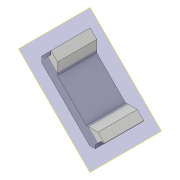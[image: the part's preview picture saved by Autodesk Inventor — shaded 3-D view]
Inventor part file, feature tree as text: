
AUTODESK INVENTOR PART (.ipt)
format: ipt  version: 2019.4 (Build 234330000, 330)  size: 292,864 bytes
history: native  units: mm
features: sketch x5, extrude x4, projected_geometry x4, emboss x2, plane x1
ambient origin geometry x8: Origin, YZ Plane, XZ Plane, XY Plane, X Axis, Y Axis, Z Axis, Center Point
bodies: Solid1 (feature_tree)
feature tree (16):
  extrude  "Extrusion1"  TaperAngle=45.0deg  [1 undecoded]
  plane  "Work Plane1"
  extrude  "Extrusion7"  Depth=30.0mm TaperAngle=0.0deg
  emboss  "Emboss1"
  emboss  "Emboss2"
  extrude  "Extrusion9"  Depth=31.0mm
  extrude  "IM_offset"  Depth=10.0mm TaperAngle=0.0deg
  sketch  "Sketch7"  dims[d0=53.8mm d1=45.0deg]
  projected_geometry  "Projected Loop3"
  sketch  "Sketch10"  dims[d2=6.28mm d3=30.0mm d4=0.0mm]
  sketch  "Sketch11"  dims[d5=8.0mm d28=31.0mm]
  projected_geometry  "Projected Loop6"
  sketch  "Sketch12"  dims[d29=1.3mm d30=10.0mm d31=0.0mm]
  projected_geometry  "Projected Loop7"
  sketch  "Sketch13"  dims[d40=1.5mm d41=1.5mm d42=1.5mm d43=10.0mm d44=10.0mm d45=1.0mm d46=0.0mm d47=120.0deg d48=1.5mm d49=1.5mm d50=1.5mm d51=1.5mm d52=1.5mm d53=0.0mm d54=60.0deg d55=1.5mm d57=120.0deg d58=1.5mm d59=120.0deg d60=1.5mm d63=2.0mm d64=0.0mm d66=10.0mm d67=0.0mm d72=24.0mm d73=45.0deg d74=0.0mm d75=8.267949mm d76=120.0deg d77=8.267949mm d78=4.160254mm d79=5.660254mm d80=120.0deg d81=120.0deg d82=3.0mm d83=3.0mm d84=3.0mm d85=1.5mm d86=7.160254mm d87=7.160254mm d88=4.160254mm d89=1.732051mm d90=5.660254mm d91=1.732051mm d92=4.160254mm d93=0.14mm]
  projected_geometry  "Projected Loop8"
note: 1 required parameter value undecoded (feature->parameter linkage not recoverable at this tier; creation-order binding heuristic only, values carry confidence <= 0.55)
